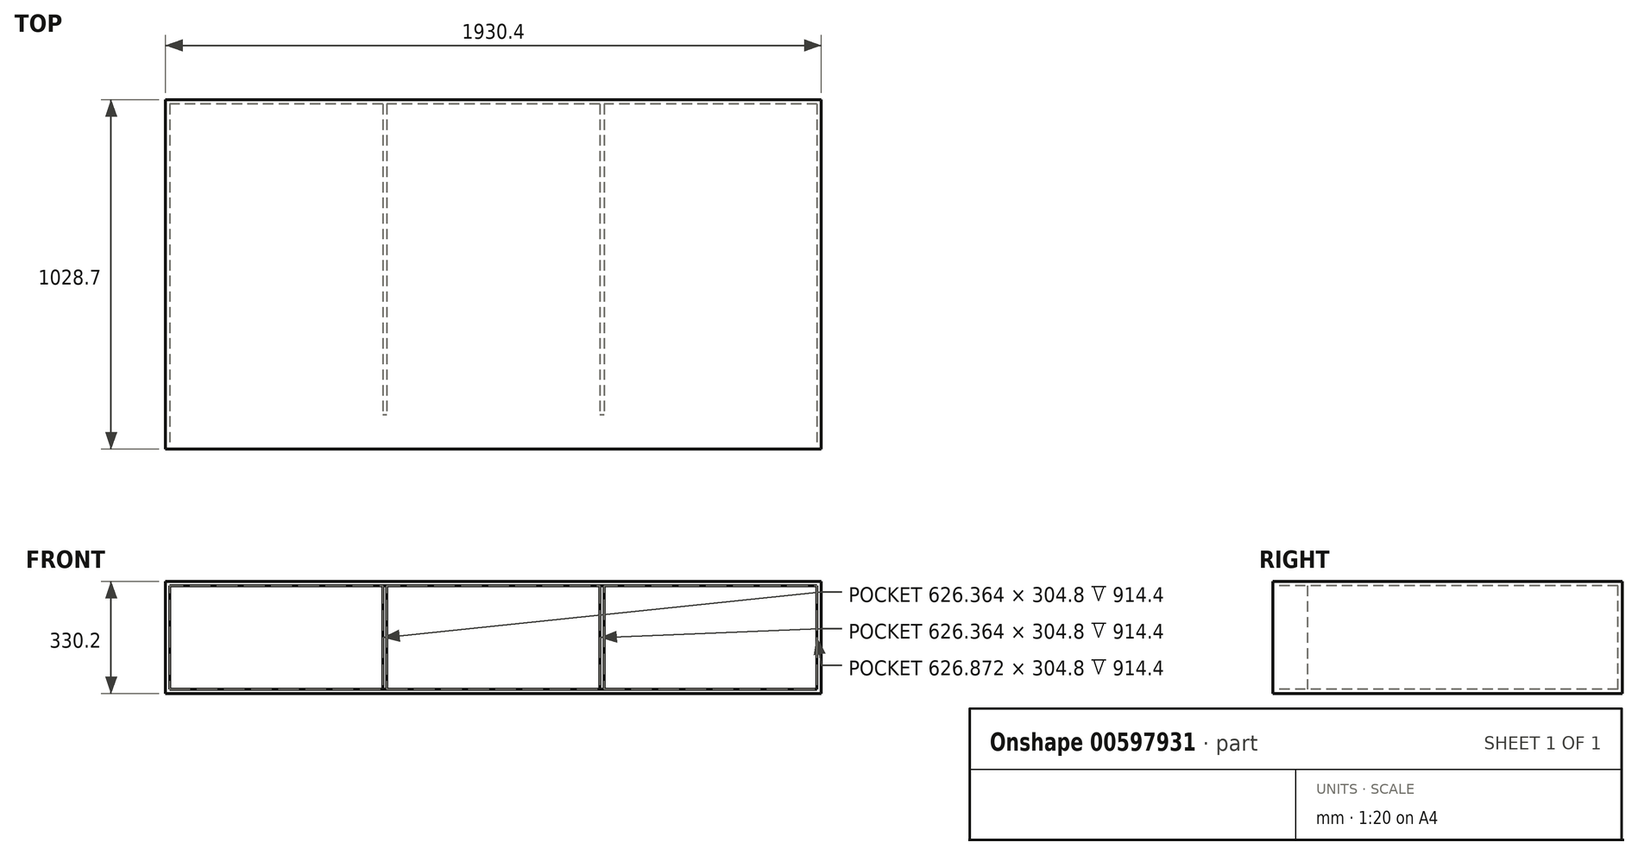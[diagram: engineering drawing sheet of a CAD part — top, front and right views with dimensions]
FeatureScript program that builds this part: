
annotation { "Feature Type Name" : "Feature", "Feature Type Description" : "" }
export const myFeature = defineFeature(function(context is Context, id is Id, definition is map)
    precondition{}
    {
        {
            var Q0;
            Q0=qCreatedBy(makeId("Top.planeOp"),FACE);
            var sketch = newSketch(context, id + "F0", { "sketchPlane" : qUnion([Q0])});
            skLineSegment(sketch, "E0.bottom", {"start": v(0, 0) * mm, "end": v(1930.4, 0) * mm});
            skLineSegment(sketch, "E0.top", {"start": v(0, 1028.7) * mm, "end": v(1930.4, 1028.7) * mm});
            skLineSegment(sketch, "E0.left", {"start": v(0, 0) * mm, "end": v(0, 1028.7) * mm});
            skLineSegment(sketch, "E0.right", {"start": v(1930.4, 0) * mm, "end": v(1930.4, 1028.7) * mm});
            skSolve(sketch);
        }
        {
            var Q0;
            Q0=makeQuery(id+"F0.imprint","IMPRINT",FACE,{"disambiguationData":[TD([[makeQuery(id+"F0.imprint","IMPRINT",EDGE,{"derivedFrom":sQuery(id+"F0.wireOp",EDGE,"E0.bottom")}),1.0]])]});
            extrude(context, id + "F1", {"entities" : qUnion([Q0]), "depth" : 12.7 * mm, "offsetDistance" : 25.4 * mm});
        }
        {
            var Q0;
            Q0=makeQuery(id+"F1.opExtrude","CAP_FACE",FACE,{"disambiguationData":[OSD([sQuery(id+"F0.wireOp",EDGE,"E0.bottom"),sQuery(id+"F0.wireOp",EDGE,"E0.top"),sQuery(id+"F0.wireOp",EDGE,"E0.left"),sQuery(id+"F0.wireOp",EDGE,"E0.right")])],"isStart":false});
            var sketch = newSketch(context, id + "F2", { "sketchPlane" : qUnion([Q0])});
            skLineSegment(sketch, "E1.bottom", {"start": v(0, 1028.7) * mm, "end": v(12.7, 1028.7) * mm});
            skLineSegment(sketch, "E1.top", {"start": v(0, 0) * mm, "end": v(12.7, 0) * mm});
            skLineSegment(sketch, "E1.left", {"start": v(0, 1028.7) * mm, "end": v(0, 0) * mm});
            skLineSegment(sketch, "E1.right", {"start": v(12.7, 1028.7) * mm, "end": v(12.7, 0) * mm});
            skLineSegment(sketch, "E2.bottom", {"start": v(1930.4, 1028.7) * mm, "end": v(1917.7, 1028.7) * mm});
            skLineSegment(sketch, "E2.top", {"start": v(1930.4, 0) * mm, "end": v(1917.7, 0) * mm});
            skLineSegment(sketch, "E2.left", {"start": v(1930.4, 1028.7) * mm, "end": v(1930.4, 0) * mm});
            skLineSegment(sketch, "E2.right", {"start": v(1917.7, 1028.7) * mm, "end": v(1917.7, 0) * mm});
            skLineSegment(sketch, "E3.bottom", {"start": v(639.06, 1028.7) * mm, "end": v(651.76, 1028.7) * mm});
            skLineSegment(sketch, "E3.top", {"start": v(639.06, 101.6) * mm, "end": v(651.76, 101.6) * mm});
            skLineSegment(sketch, "E3.left", {"start": v(639.06, 1028.7) * mm, "end": v(639.06, 101.6) * mm});
            skLineSegment(sketch, "E3.right", {"start": v(651.76, 1028.7) * mm, "end": v(651.76, 101.6) * mm});
            skLineSegment(sketch, "E4.bottom", {"start": v(1278.13, 1028.7) * mm, "end": v(1290.83, 1028.7) * mm});
            skLineSegment(sketch, "E4.top", {"start": v(1278.13, 101.6) * mm, "end": v(1290.83, 101.6) * mm});
            skLineSegment(sketch, "E4.left", {"start": v(1278.13, 1028.7) * mm, "end": v(1278.13, 101.6) * mm});
            skLineSegment(sketch, "E4.right", {"start": v(1290.83, 1028.7) * mm, "end": v(1290.83, 101.6) * mm});
            skSolve(sketch);
        }
        {
            var Q0;
            Q0 = qSketchRegion(id + "F2", true);
            extrude(context, id + "F3", {"entities" : qUnion([Q0]), "operationType" : NewBodyOperationType.ADD, "depth" : 304.8 * mm, "offsetDistance" : 25.4 * mm});
        }
        {
            var Q0;
            Q0=makeQuery(id+"F3.opExtrude","CAP_FACE",FACE,{"disambiguationData":[OSD([sQuery(id+"F2.wireOp",EDGE,"E1.bottom"),sQuery(id+"F2.wireOp",EDGE,"E1.top"),sQuery(id+"F2.wireOp",EDGE,"E1.left"),sQuery(id+"F2.wireOp",EDGE,"E1.right")])],"isStart":false});
            var sketch = newSketch(context, id + "F4", { "sketchPlane" : qUnion([Q0])});
            skLineSegment(sketch, "E5.bottom", {"start": v(0, 1028.7) * mm, "end": v(1930.4, 1028.7) * mm});
            skLineSegment(sketch, "E5.top", {"start": v(0, 0) * mm, "end": v(1930.4, 0) * mm});
            skLineSegment(sketch, "E5.left", {"start": v(0, 1028.7) * mm, "end": v(0, 0) * mm});
            skLineSegment(sketch, "E5.right", {"start": v(1930.4, 1028.7) * mm, "end": v(1930.4, 0) * mm});
            skSolve(sketch);
        }
        {
            var Q0;
            Q0 = qSketchRegion(id + "F4", true);
            extrude(context, id + "F5", {"entities" : qUnion([Q0]), "operationType" : NewBodyOperationType.ADD, "depth" : 12.7 * mm, "offsetDistance" : 25.4 * mm});
        }
        {
            var Q0;
            Q0=makeQuery(id+"F5.boolean.opBoolean","MERGE",FACE,{"derivedFrom":[makeQuery(id+"F3.boolean.opBoolean","MERGE",FACE,{"derivedFrom":[makeQuery(id+"F1.opExtrude","SWEPT_FACE",FACE,{"disambiguationData":[OSD([sQuery(id+"F0.wireOp",EDGE,"E0.top")])]}),makeQuery(id+"F3.opExtrude","SWEPT_FACE",FACE,{"disambiguationData":[OSD([sQuery(id+"F2.wireOp",EDGE,"E1.bottom")])]}),makeQuery(id+"F3.opExtrude","SWEPT_FACE",FACE,{"disambiguationData":[OSD([sQuery(id+"F2.wireOp",EDGE,"E2.bottom")])]}),makeQuery(id+"F3.opExtrude","SWEPT_FACE",FACE,{"disambiguationData":[OSD([sQuery(id+"F2.wireOp",EDGE,"WYv6In5k-gX6U-d9K4-4pAl-L7NJMSnSkuvc.bottom")])]}),makeQuery(id+"F3.opExtrude","SWEPT_FACE",FACE,{"disambiguationData":[OSD([sQuery(id+"F2.wireOp",EDGE,"Y1WyjwxU-abS5-8Zif-sfk9-xqNJQgQVLsrJ.bottom")])]})]}),makeQuery(id+"F5.opExtrude","SWEPT_FACE",FACE,{"disambiguationData":[OSD([sQuery(id+"F4.wireOp",EDGE,"E5.bottom")])]})]});
            var sketch = newSketch(context, id + "F6", { "sketchPlane" : qUnion([Q0])});
            skLineSegment(sketch, "E6.bottom", {"start": v(-1930.4, 330.2) * mm, "end": v(0, 330.2) * mm});
            skLineSegment(sketch, "E6.top", {"start": v(-1930.4, 0) * mm, "end": v(0, 0) * mm});
            skLineSegment(sketch, "E6.left", {"start": v(-1930.4, 330.2) * mm, "end": v(-1930.4, 0) * mm});
            skLineSegment(sketch, "E6.right", {"start": v(0, 330.2) * mm, "end": v(0, 0) * mm});
            skSolve(sketch);
        }
        {
            var Q0;
            Q0 = qSketchRegion(id + "F6", true);
            extrude(context, id + "F7", {"entities" : qUnion([Q0]), "operationType" : NewBodyOperationType.ADD, "oppositeDirection" : true, "depth" : 12.7 * mm, "offsetDistance" : 25.4 * mm});
        }
    });
